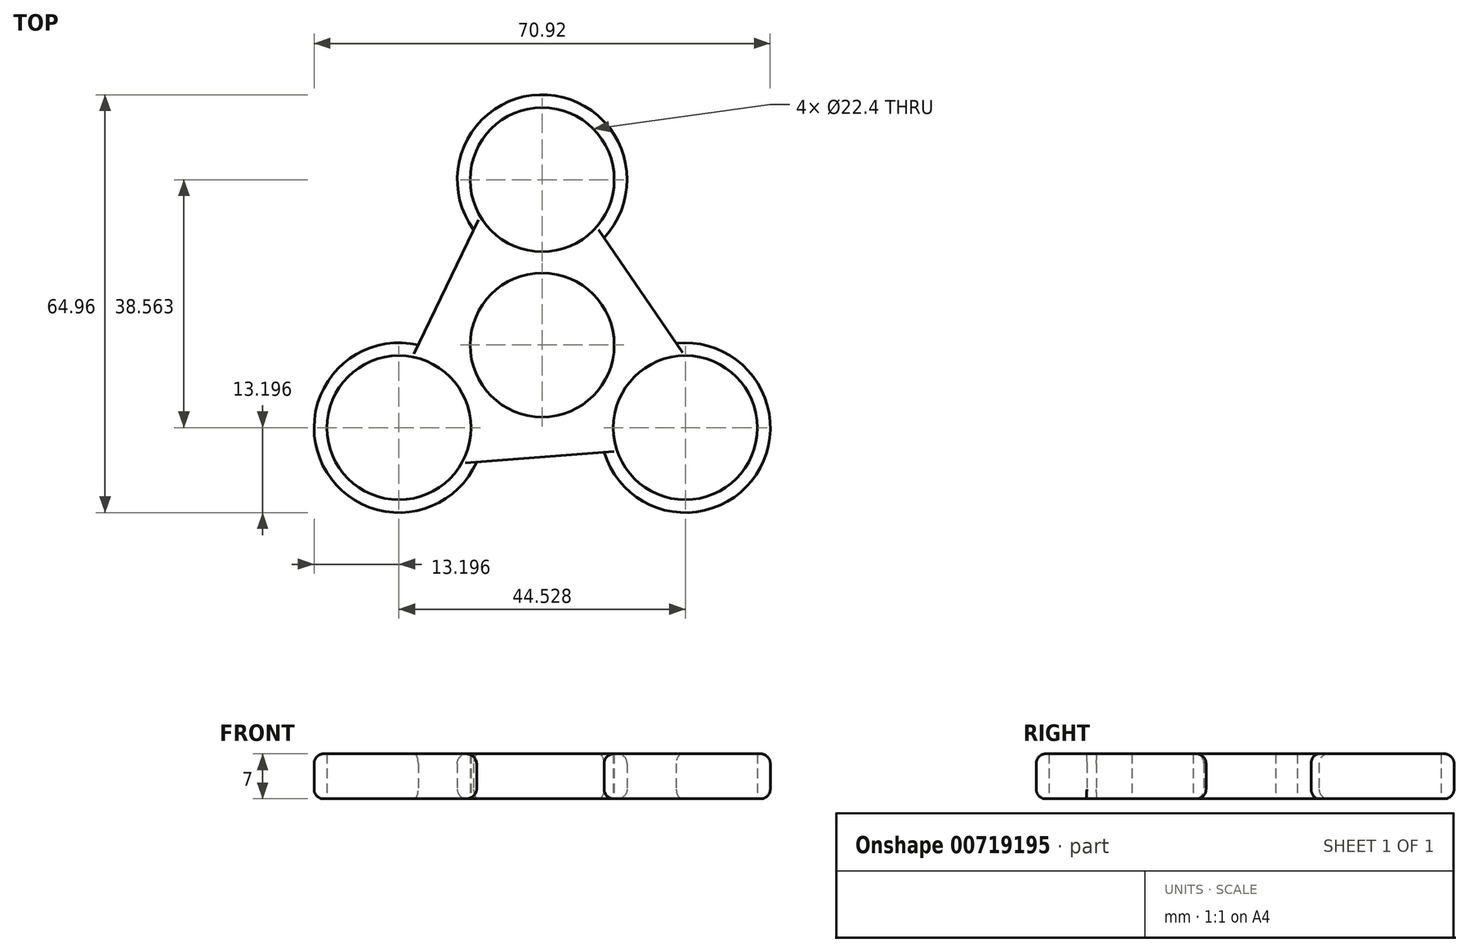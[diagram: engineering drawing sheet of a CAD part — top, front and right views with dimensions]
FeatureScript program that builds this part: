
annotation { "Feature Type Name" : "Feature", "Feature Type Description" : "" }
export const myFeature = defineFeature(function(context is Context, id is Id, definition is map)
    precondition{}
    {
        {
            var Q0;
            Q0=qCreatedBy(makeId("Top.planeOp"),FACE);
            var sketch = newSketch(context, id + "F0", { "sketchPlane" : qUnion([Q0])});
            skCircle(sketch, "E0", {"center": v(0, 0) * mm, "radius": 11.2 * mm});
            skCircle(sketch, "E1", {"center": v(0, 25.7) * mm, "radius": 11.2 * mm});
            skArc(sketch, "E2", {"start": v(9.63, 16.68) * mm, "mid": v(0.8, 38.88) * mm, "end": v(-10.66, 17.92) * mm});
            skCircle(sketch, "E3.1.0", {"center": v(-22.26, -12.85) * mm, "radius": 11.2 * mm});
            skArc(sketch, "E3.1.1", {"start": v(-19.26, 0) * mm, "mid": v(-34.08, -18.74) * mm, "end": v(-10.2, -18.2) * mm});
            skCircle(sketch, "E3.2.0", {"center": v(22.26, -12.85) * mm, "radius": 11.2 * mm});
            skArc(sketch, "E3.2.1", {"start": v(9.63, -16.68) * mm, "mid": v(33.27, -20.14) * mm, "end": v(20.85, 0.27) * mm});
            skFitSpline(sketch, "E4", {"points": [v(-10.2, -18.2) * mm, v(9.63, -16.68) * mm], "startDerivative": vector(19.82, 1.5) * mm, "endDerivative": vector(19.82, 1.5) * mm});
            skFitSpline(sketch, "E5", {"points": [v(20.85, 0.27) * mm, v(9.63, 16.68) * mm], "startDerivative": vector(-11.22, 16.41) * mm, "endDerivative": vector(-11.22, 16.41) * mm});
            skFitSpline(sketch, "E6", {"points": [v(-10.66, 17.92) * mm, v(-19.26, 0) * mm], "startDerivative": vector(-8.6, -17.92) * mm, "endDerivative": vector(-8.6, -17.92) * mm});
            skSolve(sketch);
        }
        {
            var Q0;
            Q0=makeQuery(id+"F0.imprint","IMPRINT",FACE,{"disambiguationData":[TD([[makeQuery(id+"F0.imprint","IMPRINT",EDGE,{"derivedFrom":sQuery(id+"F0.wireOp",EDGE,"E0")}),-1.0]])]});
            extrude(context, id + "F1", {"entities" : qUnion([Q0]), "depth" : 7 * mm, "offsetDistance" : 25 * mm});
        }
        {
            var Q0;
            Q0=makeQuery(id+"F1.opExtrude","CAP_EDGE",EDGE,{"disambiguationData":[OSD([sQuery(id+"F0.wireOp",EDGE,"E2")])],"isStart":false});
            var Q1;
            Q1=makeQuery(id+"F1.opExtrude","CAP_EDGE",EDGE,{"disambiguationData":[OSD([sQuery(id+"F0.wireOp",EDGE,"dced769c-64cb-4dc1-aa08-bd8c66d948bf.2.0")])],"isStart":false});
            var Q2;
            Q2=makeQuery(id+"F1.opExtrude","CAP_EDGE",EDGE,{"disambiguationData":[OSD([sQuery(id+"F0.wireOp",EDGE,"E3.2.1")])],"isStart":false});
            var Q3;
            Q3=makeQuery(id+"F1.opExtrude","CAP_EDGE",EDGE,{"disambiguationData":[OSD([sQuery(id+"F0.wireOp",EDGE,"dced769c-64cb-4dc1-aa08-bd8c66d948bf.1.0")])],"isStart":false});
            var Q4;
            Q4=makeQuery(id+"F1.opExtrude","CAP_EDGE",EDGE,{"disambiguationData":[OSD([sQuery(id+"F0.wireOp",EDGE,"E3.1.1")])],"isStart":false});
            var Q5;
            Q5=makeQuery(id+"F1.opExtrude","CAP_EDGE",EDGE,{"disambiguationData":[OSD([sQuery(id+"F0.wireOp",EDGE,"iFmcViz4-xnxW-GN5w-axlg-mXgsmjnQdyN2")])],"isStart":false});
            var Q6;
            Q6=makeQuery(id+"F1.opExtrude","CAP_EDGE",EDGE,{"disambiguationData":[OSD([sQuery(id+"F0.wireOp",EDGE,"E2")])],"isStart":true});
            var Q7;
            Q7=makeQuery(id+"F1.opExtrude","CAP_EDGE",EDGE,{"disambiguationData":[OSD([sQuery(id+"F0.wireOp",EDGE,"dced769c-64cb-4dc1-aa08-bd8c66d948bf.2.0")])],"isStart":true});
            var Q8;
            Q8=makeQuery(id+"F1.opExtrude","CAP_EDGE",EDGE,{"disambiguationData":[OSD([sQuery(id+"F0.wireOp",EDGE,"E3.2.1")])],"isStart":true});
            var Q9;
            Q9=makeQuery(id+"F1.opExtrude","CAP_EDGE",EDGE,{"disambiguationData":[OSD([sQuery(id+"F0.wireOp",EDGE,"dced769c-64cb-4dc1-aa08-bd8c66d948bf.1.0")])],"isStart":true});
            var Q10;
            Q10=makeQuery(id+"F1.opExtrude","CAP_EDGE",EDGE,{"disambiguationData":[OSD([sQuery(id+"F0.wireOp",EDGE,"E3.1.1")])],"isStart":true});
            var Q11;
            Q11=makeQuery(id+"F1.opExtrude","CAP_EDGE",EDGE,{"disambiguationData":[OSD([sQuery(id+"F0.wireOp",EDGE,"iFmcViz4-xnxW-GN5w-axlg-mXgsmjnQdyN2")])],"isStart":true});
            fillet(context, id + "F2", {"entities" : qUnion([Q0, Q1, Q2, Q3, Q4, Q5, Q6, Q7, Q8, Q9, Q10, Q11]), "radius" : 1.5 * mm, "tangentPropagation" : true, "allowEdgeOverflow" : false});
        }
    });
